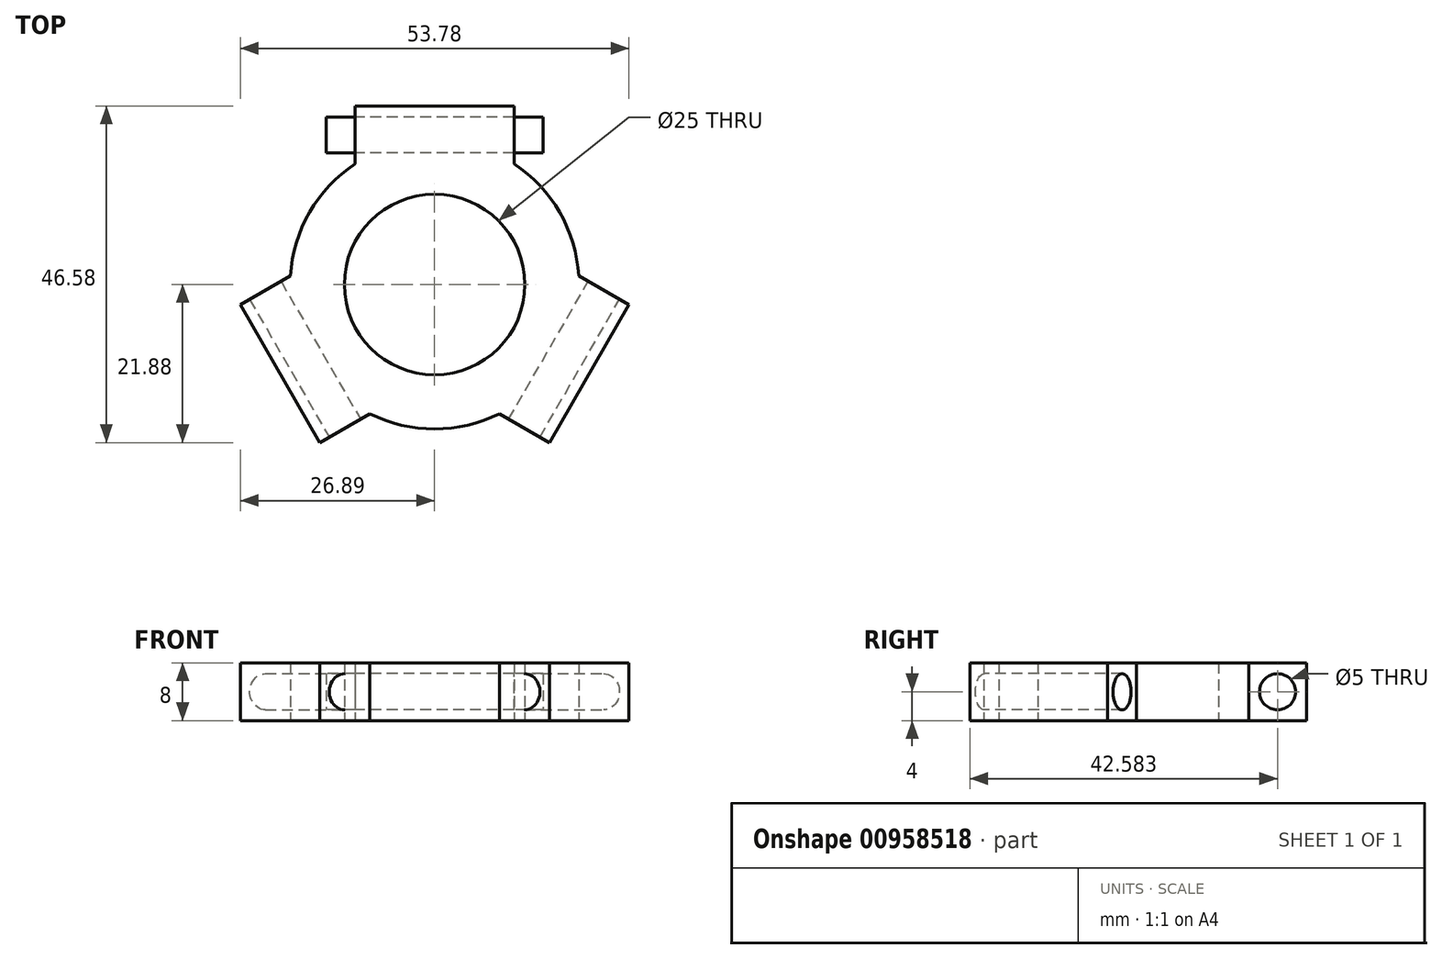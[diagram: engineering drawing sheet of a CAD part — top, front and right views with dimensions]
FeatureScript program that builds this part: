
annotation { "Feature Type Name" : "Feature", "Feature Type Description" : "" }
export const myFeature = defineFeature(function(context is Context, id is Id, definition is map)
    precondition{}
    {
        {
            var Q0;
            Q0=qCreatedBy(makeId("Top.planeOp"),FACE);
            var sketch = newSketch(context, id + "F0", { "sketchPlane" : qUnion([Q0])});
            skLineSegment(sketch, "E0", {"start": v(-11, 16.7) * mm, "end": v(-11, 24.7) * mm});
            skLineSegment(sketch, "E1", {"start": v(-11, 24.7) * mm, "end": v(11, 24.7) * mm});
            skLineSegment(sketch, "E2", {"start": v(11, 24.7) * mm, "end": v(11, 16.7) * mm});
            skLineSegment(sketch, "E3", {"start": v(11, 16.7) * mm, "end": v(19.97, 1.17) * mm, "construction": true});
            skLineSegment(sketch, "E4", {"start": v(26.9, -2.83) * mm, "end": v(19.97, 1.17) * mm});
            skLineSegment(sketch, "E5", {"start": v(26.9, -2.83) * mm, "end": v(15.9, -21.88) * mm});
            skLineSegment(sketch, "E6", {"start": v(8.97, -17.88) * mm, "end": v(15.9, -21.88) * mm});
            skLineSegment(sketch, "E7", {"start": v(8.97, -17.88) * mm, "end": v(-8.97, -17.88) * mm, "construction": true});
            skLineSegment(sketch, "E8", {"start": v(-8.97, -17.88) * mm, "end": v(-15.9, -21.88) * mm});
            skLineSegment(sketch, "E9", {"start": v(-15.9, -21.88) * mm, "end": v(-26.9, -2.83) * mm});
            skLineSegment(sketch, "E10", {"start": v(-26.9, -2.83) * mm, "end": v(-19.97, 1.17) * mm});
            skLineSegment(sketch, "E11", {"start": v(-19.97, 1.17) * mm, "end": v(-11, 16.7) * mm, "construction": true});
            skPoint(sketch, "E12", {"position": v(0, 24.7) * mm});
            skPoint(sketch, "E13", {"position": v(0, -17.88) * mm});
            skArc(sketch, "E14", {"start": v(-11, 16.7) * mm, "mid": v(-17.32, 10) * mm, "end": v(-19.97, 1.17) * mm});
            skArc(sketch, "E15", {"start": v(-19.97, 1.17) * mm, "mid": v(-17.32, -10) * mm, "end": v(-8.97, -17.88) * mm, "construction": true});
            skArc(sketch, "E16", {"start": v(-8.97, -17.88) * mm, "mid": v(0, -20) * mm, "end": v(8.97, -17.88) * mm});
            skArc(sketch, "E17", {"start": v(8.97, -17.88) * mm, "mid": v(17.32, -10) * mm, "end": v(19.97, 1.17) * mm, "construction": true});
            skArc(sketch, "E18", {"start": v(19.97, 1.17) * mm, "mid": v(17.32, 10) * mm, "end": v(11, 16.7) * mm});
            skArc(sketch, "E19", {"start": v(11, 16.7) * mm, "mid": v(0, 20) * mm, "end": v(-11, 16.7) * mm, "construction": true});
            skCircle(sketch, "E20", {"center": v(0, 0) * mm, "radius": 12.5 * mm});
            skSolve(sketch);
        }
        {
            var Q0;
            Q0=makeQuery(id+"F0.imprint","IMPRINT",FACE,{"disambiguationData":[TD([[makeQuery(id+"F0.imprint","IMPRINT",EDGE,{"derivedFrom":sQuery(id+"F0.wireOp",EDGE,"E0")}),-1.0]])]});
            extrude(context, id + "F1", {"entities" : qUnion([Q0]), "depth" : 8 * mm, "offsetDistance" : 25 * mm});
        }
        {
            var Q0;
            Q0=makeQuery(id+"F1.opExtrude","SWEPT_FACE",FACE,{"disambiguationData":[OSD([sQuery(id+"F0.wireOp",EDGE,"E0")])]});
            var sketch = newSketch(context, id + "F2", { "sketchPlane" : qUnion([Q0])});
            skLineSegment(sketch, "E21", {"start": v(-24.7, 8) * mm, "end": v(-16.7, 0) * mm, "construction": true});
            skLineSegment(sketch, "E22", {"start": v(-16.7, 8) * mm, "end": v(-24.7, 0) * mm, "construction": true});
            skPoint(sketch, "E23", {"position": v(-20.7, 4) * mm});
            skCircle(sketch, "E24", {"center": v(-20.7, 4) * mm, "radius": 2.5 * mm});
            skSolve(sketch);
        }
        {
            var Q0;
            Q0=makeQuery(id+"F2.imprint","IMPRINT",FACE,{"disambiguationData":[TD([[makeQuery(id+"F2.imprint","IMPRINT",EDGE,{"derivedFrom":sQuery(id+"F2.wireOp",EDGE,"E24")}),1.0]])]});
            extrude(context, id + "F3", {"entities" : qUnion([Q0]), "oppositeDirection" : true, "depth" : 26 * mm, "offsetDistance" : 25 * mm, "hasSecondDirection" : true, "secondDirectionOppositeDirection" : false, "secondDirectionDepth" : 4 * mm});
        }
        {
            var Q0;
            Q0=makeQuery(id+"F2.imprint","IMPRINT",FACE,{"disambiguationData":[TD([[makeQuery(id+"F2.imprint","IMPRINT",EDGE,{"derivedFrom":sQuery(id+"F2.wireOp",EDGE,"E24")}),1.0]])]});
            extrude(context, id + "F4", {"entities" : qUnion([Q0]), "endBound" : BoundingType.UP_TO_NEXT, "oppositeDirection" : true, "depth" : 25 * mm, "offsetDistance" : 25 * mm});
        }
        {
            var Q0;
            Q0=qCreatedBy(makeId("Right.planeOp"),FACE);
            var sketch = newSketch(context, id + "F5", { "sketchPlane" : qUnion([Q0])});
            skLineSegment(sketch, "E25", {"start": v(0, 0) * mm, "end": v(0, 27.57) * mm});
            skSolve(sketch);
        }
        {
            var Q0;
            Q0=makeQuery(id+"F4.opExtrude","SWEPT_BODY",BODY,{"disambiguationData":[OSD([sQuery(id+"F2.wireOp",EDGE,"E24")])]});
            var Q1;
            Q1=sQuery(id+"F5.wireOp",EDGE,"E25");
            circularPattern(context, id + "F6", {"operationType" : NewBodyOperationType.REMOVE, "entities" : qUnion([Q0]), "axis" : qUnion([Q1]), "angle" : 360 * degree, "instanceCount" : 3, "equalSpace" : true});
        }
    });
